# Revit family: QF_Marco_1000869_Friia-2B-305
name_source: partatom
category: Specialty Equipment
units: mm (PartAtom-declared; Revit-internal decimal feet)

## family parameters
Always vertical = Yes
Cut with Voids When Loaded = No
Part Type = Normal
Room Calculation Point = No
Round Connector Dimension = Use Diameter
Shared = No
Work Plane-Based = No

## types (1)
- QF_Marco_1000869_Friia-2B-305
    Cold Water Connection Height = 0 "
    Cold Water Flow = 0 GPM
    Cold Water Maximum Pressure = 0.00 psi
    Cold Water Minimum Pressure = 0.00 psi
    Cold Water RI Height = 0 "
    Cold Water Size = 0"
    Cold Water Temperature Recommended = -460 °F
    Depth = 5.433 "
    Description = Friia 2b 305
    Foodservice Equipment Identifier = Yes
    Height = 13.386 "
    Hot Water Connection Height = 0 "
    Hot Water Consumption = 0 GPM
    Hot Water Flow = 0 GPM
    Hot Water Maximum Pressure = 0.00 psi
    Hot Water Minimum Pressure = 0.00 psi
    Hot Water RI Height = 0 "
    Hot Water Size = 0"
    Hot Water Temperature = -460 °F
    Identify Quantity as Lot = Yes
    Indirect Waste Connection Height = 0 "
    Indirect Waste Flow = 0 GPM
    Indirect Waste Size = 0"
    Length = 4.75 "
    Manufacturer = Marco
    Model = 1000869
    Waste Water Discharge Temperature = -460 °F
    Weight in Pounds = 0

## geometry (parser evidence)
native form markers: Sweep x2
no freeform markers — native parametric forms only
